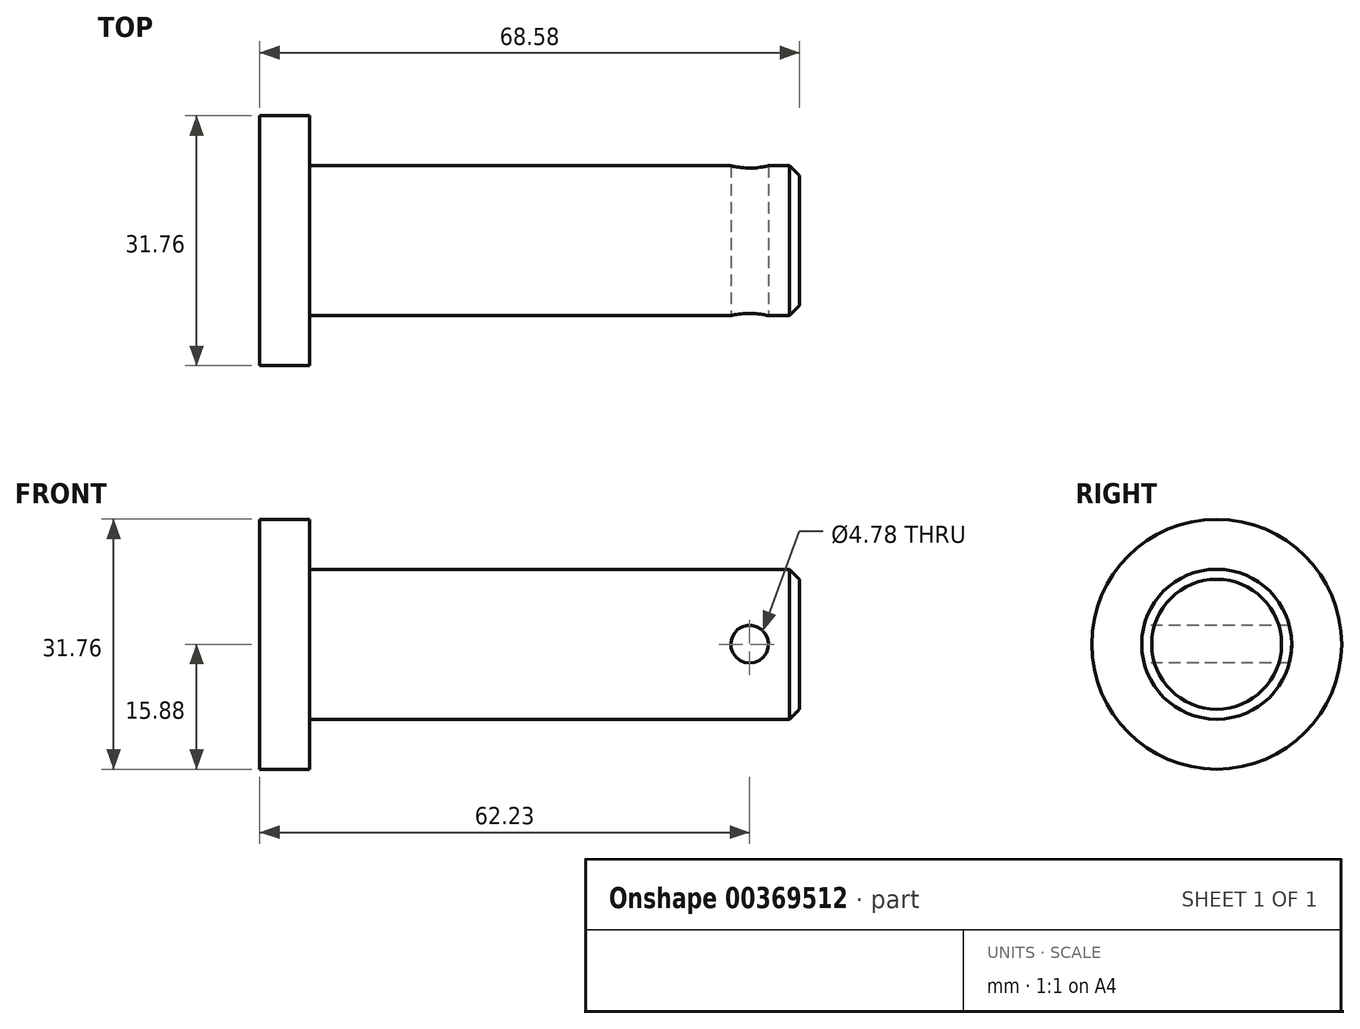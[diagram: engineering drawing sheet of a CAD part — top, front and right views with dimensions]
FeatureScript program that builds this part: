
annotation { "Feature Type Name" : "Feature", "Feature Type Description" : "" }
export const myFeature = defineFeature(function(context is Context, id is Id, definition is map)
    precondition{}
    {
        {
            var Q0;
            Q0=qCreatedBy(makeId("Right.planeOp"),FACE);
            var sketch = newSketch(context, id + "F0", { "sketchPlane" : qUnion([Q0])});
            skCircle(sketch, "E0", {"center": v(0, 0) * mm, "radius": 15.88 * mm});
            skCircle(sketch, "E1", {"center": v(0, 0) * mm, "radius": 9.53 * mm});
            skSolve(sketch);
        }
        {
            var Q0;
            Q0=makeQuery(id+"F0.imprint","IMPRINT",FACE,{"disambiguationData":[TD([[makeQuery(id+"F0.imprint","IMPRINT",EDGE,{"derivedFrom":sQuery(id+"F0.wireOp",EDGE,"E0")}),1.0]])]});
            extrude(context, id + "F1", {"entities" : qUnion([Q0]), "depth" : 6.35 * mm});
        }
        {
            var Q0;
            Q0=makeQuery(id+"F0.imprint","IMPRINT",FACE,{"disambiguationData":[TD([[makeQuery(id+"F0.imprint","IMPRINT",EDGE,{"derivedFrom":sQuery(id+"F0.wireOp",EDGE,"E1")}),1.0]])]});
            extrude(context, id + "F2", {"entities" : qUnion([Q0]), "operationType" : NewBodyOperationType.ADD, "depth" : 68.58 * mm});
        }
        {
            var Q0;
            Q0=qCreatedBy(makeId("Front.planeOp"),FACE);
            var sketch = newSketch(context, id + "F3", { "sketchPlane" : qUnion([Q0])});
            skLineSegment(sketch, "E2", {"start": v(0, 0) * mm, "end": v(82.6, 0) * mm, "construction": true});
            skCircle(sketch, "E3", {"center": v(62.23, 0) * mm, "radius": 2.39 * mm});
            skSolve(sketch);
        }
        {
            var Q0;
            Q0 = qSketchRegion(id + "F3", true);
            extrude(context, id + "F4", {"entities" : qUnion([Q0]), "operationType" : NewBodyOperationType.REMOVE, "endBound" : BoundingType.SYMMETRIC, "oppositeDirection" : true, "depth" : 25.4 * mm});
        }
        {
            var Q0;
            Q0=makeQuery(id+"F2.opExtrude","CAP_EDGE",EDGE,{"disambiguationData":[OSD([sQuery(id+"F0.wireOp",EDGE,"E1")])],"isStart":false});
            chamfer(context, id + "F5", {"entities" : qUnion([Q0]), "chamferType" : ChamferType.OFFSET_ANGLE, "width" : 1.27 * mm, "oppositeDirection" : false, "angle" : 45 * degree, "tangentPropagation" : true});
        }
    });
